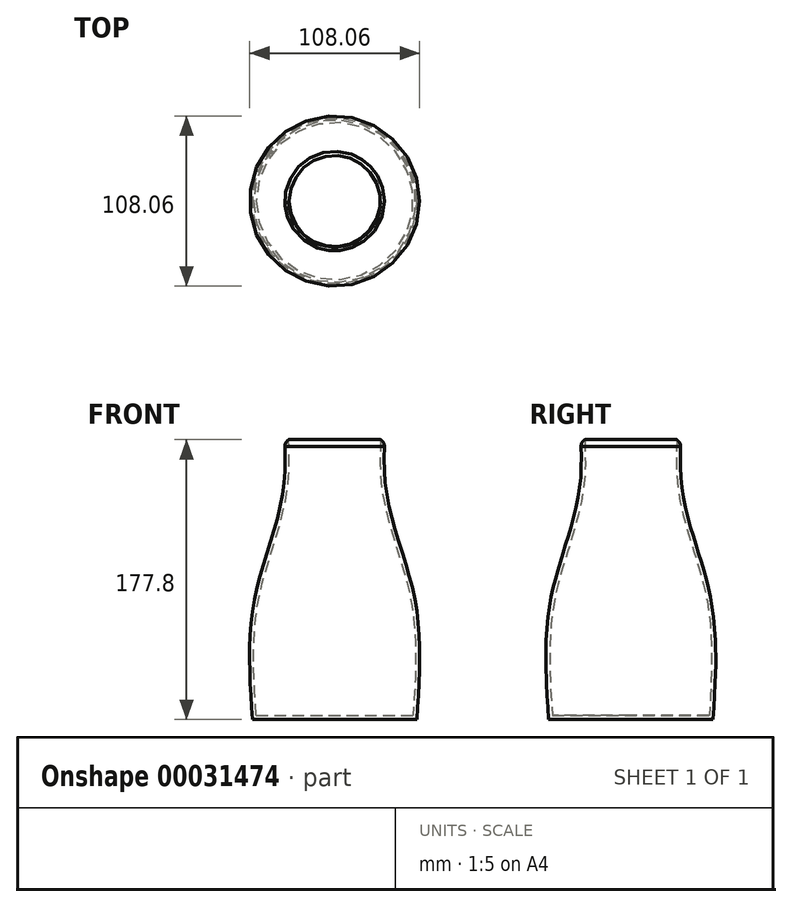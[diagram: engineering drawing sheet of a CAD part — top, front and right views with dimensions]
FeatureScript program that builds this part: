
annotation { "Feature Type Name" : "Feature", "Feature Type Description" : "" }
export const myFeature = defineFeature(function(context is Context, id is Id, definition is map)
    precondition{}
    {
        {
            var Q0;
            Q0=qCreatedBy(makeId("Top.planeOp"),FACE);
            var sketch = newSketch(context, id + "F0", { "sketchPlane" : qUnion([Q0])});
            skCircle(sketch, "E0", {"center": v(0, 0) * mm, "radius": 31.75 * mm});
            skSolve(sketch);
        }
        {
            var Q0;
            Q0=qCreatedBy(makeId("Top.planeOp"),FACE);
            cPlane(context, id + "F1", {"entities" : qUnion([Q0]), "cplaneType" : CPlaneType.OFFSET, "offset" : 38.1 * mm, "oppositeDirection" : true, "width" : 152.4 * mm, "height" : 152.4 * mm});
        }
        {
            var Q0;
            Q0=qCreatedBy(makeId("Top.planeOp"),FACE);
            cPlane(context, id + "F2", {"entities" : qUnion([Q0]), "cplaneType" : CPlaneType.OFFSET, "offset" : 25.4 * mm, "oppositeDirection" : true, "width" : 152.4 * mm, "height" : 152.4 * mm});
        }
        {
            var Q0;
            Q0=qCreatedBy(makeId("Top.planeOp"),FACE);
            cPlane(context, id + "F3", {"entities" : qUnion([Q0]), "cplaneType" : CPlaneType.OFFSET, "offset" : 177.8 * mm, "oppositeDirection" : true, "width" : 152.4 * mm, "height" : 152.4 * mm});
        }
        {
            var Q0;
            Q0=qCreatedBy(id+"F2.planeOp",FACE);
            var sketch = newSketch(context, id + "F4", { "sketchPlane" : qUnion([Q0])});
            skCircle(sketch, "E1", {"center": v(0, 0) * mm, "radius": 31.9 * mm});
            skSolve(sketch);
        }
        {
            var Q0;
            Q0=qCreatedBy(id+"F3.planeOp",FACE);
            var sketch = newSketch(context, id + "F5", { "sketchPlane" : qUnion([Q0])});
            skCircle(sketch, "E2", {"center": v(0, 0) * mm, "radius": 52.2 * mm});
            skSolve(sketch);
        }
        {
            var Q0;
            Q0=qCreatedBy(makeId("Top.planeOp"),FACE);
            cPlane(context, id + "F6", {"entities" : qUnion([Q0]), "cplaneType" : CPlaneType.OFFSET, "offset" : 101.6 * mm, "oppositeDirection" : true, "width" : 152.4 * mm, "height" : 152.4 * mm});
        }
        {
            var Q0;
            Q0=qCreatedBy(id+"F6.planeOp",FACE);
            var sketch = newSketch(context, id + "F7", { "sketchPlane" : qUnion([Q0])});
            skCircle(sketch, "E3", {"center": v(0, 0) * mm, "radius": 50.94 * mm});
            skSolve(sketch);
        }
        {
            var Q0;
            Q0=makeQuery(id+"F5.imprint","IMPRINT",FACE,{"disambiguationData":[TD([[makeQuery(id+"F5.imprint","IMPRINT",EDGE,{"derivedFrom":sQuery(id+"F5.wireOp",EDGE,"E2")}),1.0]])]});
            var Q1;
            Q1=makeQuery(id+"F7.imprint","IMPRINT",FACE,{"disambiguationData":[TD([[makeQuery(id+"F7.imprint","IMPRINT",EDGE,{"derivedFrom":sQuery(id+"F7.wireOp",EDGE,"E3")}),1.0]])]});
            var Q2;
            Q2=makeQuery(id+"F4.imprint","IMPRINT",FACE,{"disambiguationData":[TD([[makeQuery(id+"F4.imprint","IMPRINT",EDGE,{"derivedFrom":sQuery(id+"F4.wireOp",EDGE,"E1")}),1.0]])]});
            var Q3;
            Q3=makeQuery(id+"F0.imprint","IMPRINT",FACE,{"disambiguationData":[TD([[makeQuery(id+"F0.imprint","IMPRINT",EDGE,{"derivedFrom":sQuery(id+"F0.wireOp",EDGE,"E0")}),1.0]])]});
            loft(context, id + "F8", {"sheetProfilesArray" : [{ "sheetProfileEntities" : qUnion([Q0]) }, { "sheetProfileEntities" : qUnion([Q1]) }, { "sheetProfileEntities" : qUnion([Q2]) }, { "sheetProfileEntities" : qUnion([Q3]) }]});
        }
        {
            var Q0;
            Q0=makeQuery(id+"F8.opLoft","CAP_FACE",FACE,{"disambiguationData":[OSD([makeQuery(id+"F0.imprint","IMPRINT",FACE,{"disambiguationData":[TD([[makeQuery(id+"F0.imprint","IMPRINT",EDGE,{"derivedFrom":sQuery(id+"F0.wireOp",EDGE,"E0")}),1.0]])]})])],"isStart":true});
            shell(context, id + "F9", {"entities" : qUnion([Q0]), "thickness" : 2.54 * mm});
        }
        {
            var Q0;
            Q0=makeQuery(id+"F8.opLoft","MID_CAP_EDGE",EDGE,{"disambiguationData":[OSD([sQuery(id+"F0.wireOp",EDGE,"E0"),sQuery(id+"F5.wireOp",EDGE,"E2")])],"capPos":3.0});
            fillet(context, id + "F10", {"entities" : qUnion([Q0]), "radius" : 5.08 * mm, "tangentPropagation" : true, "allowEdgeOverflow" : false});
        }
    });
